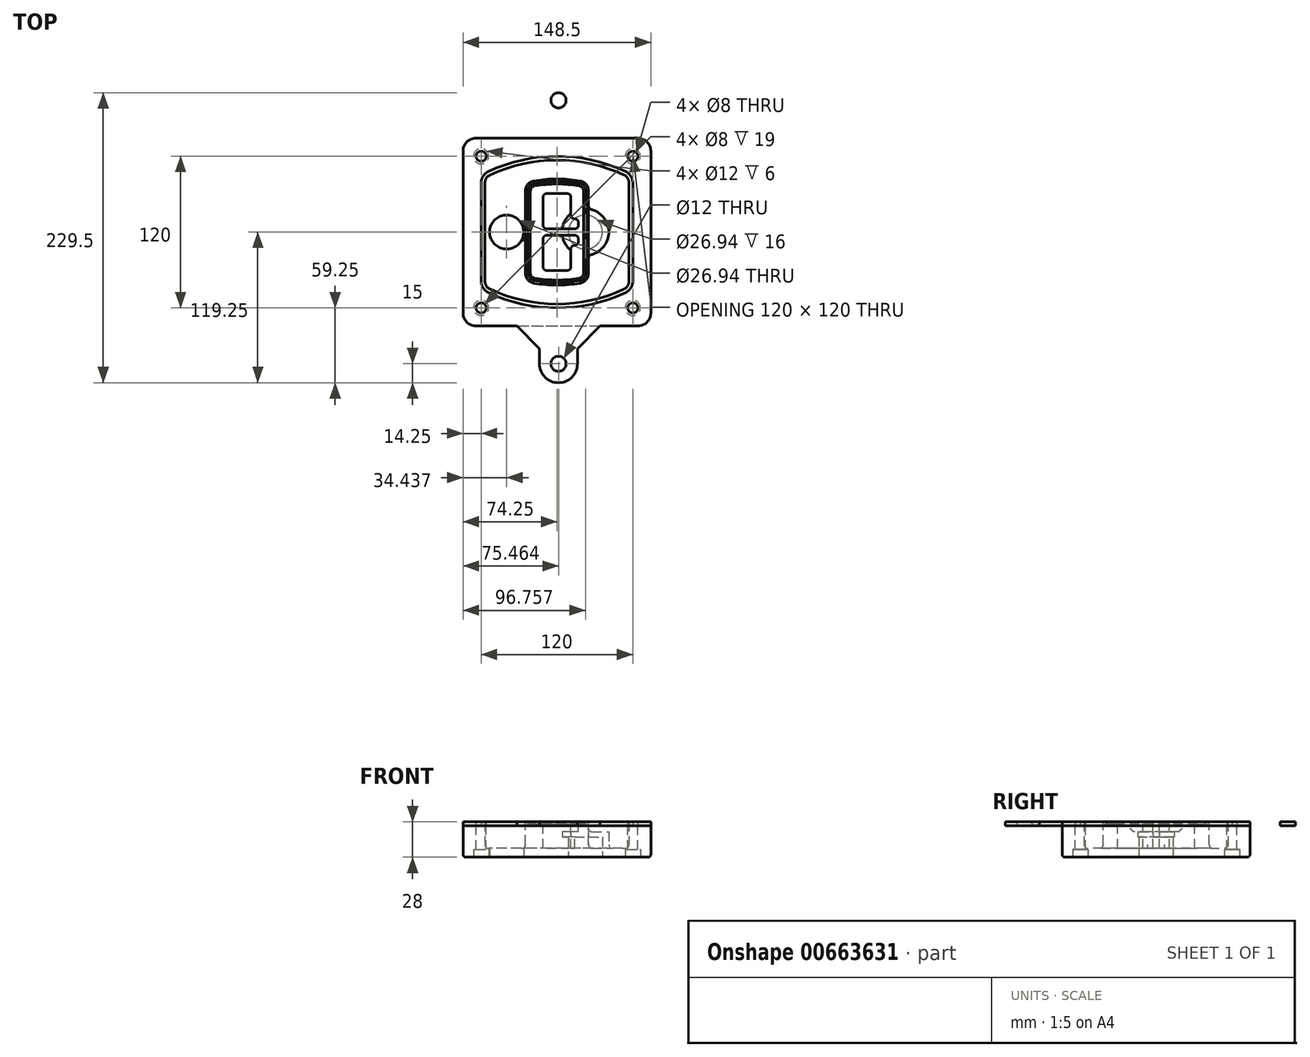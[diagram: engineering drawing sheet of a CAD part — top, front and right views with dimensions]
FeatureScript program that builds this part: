
annotation { "Feature Type Name" : "Feature", "Feature Type Description" : "" }
export const myFeature = defineFeature(function(context is Context, id is Id, definition is map)
    precondition{}
    {
        {
            var Q0;
            Q0=qCreatedBy(makeId("Top.planeOp"),FACE);
            var sketch = newSketch(context, id + "F0", { "sketchPlane" : qUnion([Q0])});
            skPoint(sketch, "E0.rect.middle", {"position": v(0, 0) * mm});
            skLineSegment(sketch, "E1.bottom", {"start": v(-64.25, -74.25) * mm, "end": v(64.25, -74.25) * mm});
            skLineSegment(sketch, "E1.top", {"start": v(-64.25, 74.25) * mm, "end": v(64.25, 74.25) * mm});
            skLineSegment(sketch, "E1.left", {"start": v(-74.25, -64.25) * mm, "end": v(-74.25, 64.25) * mm});
            skLineSegment(sketch, "E1.right", {"start": v(74.25, -64.25) * mm, "end": v(74.25, 64.25) * mm});
            skLineSegment(sketch, "E2", {"start": v(-74.25, 74.25) * mm, "end": v(74.25, -74.25) * mm, "construction": true});
            skLineSegment(sketch, "E3", {"start": v(74.25, 74.25) * mm, "end": v(-74.25, -74.25) * mm, "construction": true});
            skCircle(sketch, "E4", {"center": v(-60, 60) * mm, "radius": 4 * mm});
            skCircle(sketch, "E5", {"center": v(60, 60) * mm, "radius": 4 * mm});
            skCircle(sketch, "E6", {"center": v(60, -60) * mm, "radius": 4 * mm});
            skCircle(sketch, "E7", {"center": v(-60, -60) * mm, "radius": 4 * mm});
            skLineSegment(sketch, "E8", {"start": v(-60, 60) * mm, "end": v(60, 60) * mm, "construction": true});
            skLineSegment(sketch, "E9", {"start": v(60, 60) * mm, "end": v(60, -60) * mm, "construction": true});
            skLineSegment(sketch, "E10", {"start": v(60, -60) * mm, "end": v(-60, -60) * mm, "construction": true});
            skLineSegment(sketch, "E11", {"start": v(-60, -60) * mm, "end": v(-60, 60) * mm, "construction": true});
            skLineSegment(sketch, "E12", {"start": v(-60, 38.83) * mm, "end": v(-60, -38.83) * mm});
            skLineSegment(sketch, "E13", {"start": v(60, 38.83) * mm, "end": v(60, -38.83) * mm});
            skArc(sketch, "E14", {"start": v(54.26, 47.88) * mm, "mid": v(0, 60) * mm, "end": v(-54.26, 47.88) * mm});
            skArc(sketch, "E15", {"start": v(-54.26, -47.88) * mm, "mid": v(0, -60) * mm, "end": v(54.26, -47.88) * mm});
            skLineSegment(sketch, "E16", {"start": v(-60, 0) * mm, "end": v(60, 0) * mm, "construction": true});
            skPoint(sketch, "E17.visualSharp", {"position": v(-60, -45) * mm});
            skArc(sketch, "E17.filletArc", {"start": v(-60, -38.83) * mm, "mid": v(-58.44, -44.2) * mm, "end": v(-54.26, -47.88) * mm});
            skPoint(sketch, "E18.visualSharp", {"position": v(-60, 45) * mm});
            skArc(sketch, "E18.filletArc", {"start": v(-54.26, 47.88) * mm, "mid": v(-58.44, 44.2) * mm, "end": v(-60, 38.83) * mm});
            skPoint(sketch, "E19.visualSharp", {"position": v(60, 45) * mm});
            skArc(sketch, "E19.filletArc", {"start": v(60, 38.83) * mm, "mid": v(58.44, 44.2) * mm, "end": v(54.26, 47.88) * mm});
            skPoint(sketch, "E20.visualSharp", {"position": v(60, -45) * mm});
            skArc(sketch, "E20.filletArc", {"start": v(54.26, -47.88) * mm, "mid": v(58.44, -44.2) * mm, "end": v(60, -38.83) * mm});
            skPoint(sketch, "E21.visualSharp", {"position": v(-74.25, 74.25) * mm});
            skArc(sketch, "E21.filletArc", {"start": v(-64.25, 74.25) * mm, "mid": v(-71.32, 71.32) * mm, "end": v(-74.25, 64.25) * mm});
            skPoint(sketch, "E22.visualSharp", {"position": v(74.25, 74.25) * mm});
            skArc(sketch, "E22.filletArc", {"start": v(74.25, 64.25) * mm, "mid": v(71.32, 71.32) * mm, "end": v(64.25, 74.25) * mm});
            skPoint(sketch, "E23.visualSharp", {"position": v(74.25, -74.25) * mm});
            skArc(sketch, "E23.filletArc", {"start": v(64.25, -74.25) * mm, "mid": v(71.32, -71.32) * mm, "end": v(74.25, -64.25) * mm});
            skPoint(sketch, "E24.visualSharp", {"position": v(-74.25, -74.25) * mm});
            skArc(sketch, "E24.filletArc", {"start": v(-74.25, -64.25) * mm, "mid": v(-71.32, -71.32) * mm, "end": v(-64.25, -74.25) * mm});
            skArc(sketch, "E25.0", {"start": v(57, 38.83) * mm, "mid": v(55.9, 42.58) * mm, "end": v(52.98, 45.17) * mm});
            skLineSegment(sketch, "E25.1", {"start": v(57, 38.83) * mm, "end": v(57, -38.83) * mm});
            skArc(sketch, "E25.2", {"start": v(52.98, -45.17) * mm, "mid": v(55.9, -42.58) * mm, "end": v(57, -38.83) * mm});
            skArc(sketch, "E25.3", {"start": v(-52.98, -45.17) * mm, "mid": v(0, -57) * mm, "end": v(52.98, -45.17) * mm});
            skArc(sketch, "E25.4", {"start": v(-57, -38.83) * mm, "mid": v(-55.9, -42.58) * mm, "end": v(-52.98, -45.17) * mm});
            skArc(sketch, "E25.5", {"start": v(52.98, 45.17) * mm, "mid": v(0, 57) * mm, "end": v(-52.98, 45.17) * mm});
            skLineSegment(sketch, "E25.6", {"start": v(-57, 38.83) * mm, "end": v(-57, -38.83) * mm});
            skArc(sketch, "E25.7", {"start": v(-52.98, 45.17) * mm, "mid": v(-55.9, 42.58) * mm, "end": v(-57, 38.83) * mm});
            skArc(sketch, "E26.0", {"start": v(-55.96, 51.5) * mm, "mid": v(-61.82, 46.33) * mm, "end": v(-64, 38.83) * mm});
            skArc(sketch, "E26.1", {"start": v(55.96, 51.5) * mm, "mid": v(0, 64) * mm, "end": v(-55.96, 51.5) * mm});
            skArc(sketch, "E26.2", {"start": v(64, 38.83) * mm, "mid": v(61.82, 46.33) * mm, "end": v(55.96, 51.5) * mm});
            skLineSegment(sketch, "E26.3", {"start": v(64, 38.83) * mm, "end": v(64, -38.83) * mm});
            skArc(sketch, "E26.4", {"start": v(55.96, -51.5) * mm, "mid": v(61.82, -46.33) * mm, "end": v(64, -38.83) * mm});
            skLineSegment(sketch, "E26.5", {"start": v(-64, 38.83) * mm, "end": v(-64, -38.83) * mm});
            skArc(sketch, "E26.6", {"start": v(-55.96, -51.5) * mm, "mid": v(0, -64) * mm, "end": v(55.96, -51.5) * mm});
            skArc(sketch, "E26.7", {"start": v(-64, -38.83) * mm, "mid": v(-61.82, -46.33) * mm, "end": v(-55.96, -51.5) * mm});
            skSolve(sketch);
        }
        {
            var Q0;
            Q0=makeQuery(id+"F0.imprint","IMPRINT",FACE,{"disambiguationData":[TD([[makeQuery(id+"F0.imprint","IMPRINT",EDGE,{"derivedFrom":sQuery(id+"F0.wireOp",EDGE,"E1.bottom")}),1.0]])]});
            var Q1;
            Q1=makeQuery(id+"F0.imprint","IMPRINT",FACE,{"disambiguationData":[TD([[makeQuery(id+"F0.imprint","IMPRINT",EDGE,{"derivedFrom":sQuery(id+"F0.wireOp",EDGE,"E12")}),1.0]])]});
            var Q2;
            Q2=makeQuery(id+"F0.imprint","IMPRINT",FACE,{"disambiguationData":[TD([[makeQuery(id+"F0.imprint","IMPRINT",EDGE,{"derivedFrom":sQuery(id+"F0.wireOp",EDGE,"E25.0")}),1.0]])]});
            var Q3;
            Q3=makeQuery(id+"F0.imprint","IMPRINT",FACE,{"disambiguationData":[TD([[makeQuery(id+"F0.imprint","IMPRINT",EDGE,{"derivedFrom":sQuery(id+"F0.wireOp",EDGE,"E12")}),-1.0]])]});
            extrude(context, id + "F1", {"entities" : qUnion([Q0, Q1, Q2, Q3]), "oppositeDirection" : true, "depth" : 25 * mm});
        }
        {
            var Q0;
            Q0=makeQuery(id+"F0.imprint","IMPRINT",FACE,{"disambiguationData":[TD([[makeQuery(id+"F0.imprint","IMPRINT",EDGE,{"derivedFrom":sQuery(id+"F0.wireOp",EDGE,"E12")}),1.0]])]});
            extrude(context, id + "F2", {"entities" : qUnion([Q0]), "operationType" : NewBodyOperationType.ADD, "depth" : 3 * mm});
        }
        {
            var Q0;
            Q0=makeQuery(id+"F0.imprint","IMPRINT",FACE,{"disambiguationData":[TD([[makeQuery(id+"F0.imprint","IMPRINT",EDGE,{"derivedFrom":sQuery(id+"F0.wireOp",EDGE,"E25.0")}),1.0]])]});
            extrude(context, id + "F3", {"entities" : qUnion([Q0]), "operationType" : NewBodyOperationType.REMOVE, "oppositeDirection" : true, "depth" : 18 * mm});
        }
        {
            var Q0;
            Q0=makeQuery(id+"F2.opExtrude","CAP_FACE",FACE,{"disambiguationData":[OSD([sQuery(id+"F0.wireOp",EDGE,"E12"),sQuery(id+"F0.wireOp",EDGE,"E13"),sQuery(id+"F0.wireOp",EDGE,"E14"),sQuery(id+"F0.wireOp",EDGE,"E15"),sQuery(id+"F0.wireOp",EDGE,"E17.filletArc"),sQuery(id+"F0.wireOp",EDGE,"E18.filletArc"),sQuery(id+"F0.wireOp",EDGE,"E19.filletArc"),sQuery(id+"F0.wireOp",EDGE,"E20.filletArc"),sQuery(id+"F0.wireOp",EDGE,"E25.0"),sQuery(id+"F0.wireOp",EDGE,"E25.1"),sQuery(id+"F0.wireOp",EDGE,"E25.2"),sQuery(id+"F0.wireOp",EDGE,"E25.3"),sQuery(id+"F0.wireOp",EDGE,"E25.4"),sQuery(id+"F0.wireOp",EDGE,"E25.5"),sQuery(id+"F0.wireOp",EDGE,"E25.6"),sQuery(id+"F0.wireOp",EDGE,"E25.7")])],"isStart":false});
            var sketch = newSketch(context, id + "F4", { "sketchPlane" : qUnion([Q0])});
            skArc(sketch, "E27.0", {"start": v(-18.34, -40.45) * mm, "mid": v(0, -42) * mm, "end": v(18.34, -40.45) * mm});
            skArc(sketch, "E28.0", {"start": v(18.34, 40.45) * mm, "mid": v(0, 42) * mm, "end": v(-18.34, 40.45) * mm});
            skLineSegment(sketch, "E29", {"start": v(-25, 32.57) * mm, "end": v(-25, -32.57) * mm});
            skLineSegment(sketch, "E30", {"start": v(25, 32.57) * mm, "end": v(25, -32.57) * mm});
            skLineSegment(sketch, "E31", {"start": v(-25, 39.1) * mm, "end": v(25, 39.1) * mm, "construction": true});
            skLineSegment(sketch, "E32", {"start": v(-25, -39.1) * mm, "end": v(25, -39.1) * mm, "construction": true});
            skPoint(sketch, "E33.visualSharp", {"position": v(-25, 39.1) * mm});
            skArc(sketch, "E33.filletArc", {"start": v(-18.34, 40.45) * mm, "mid": v(-23.11, 37.73) * mm, "end": v(-25, 32.57) * mm});
            skPoint(sketch, "E34.visualSharp", {"position": v(25, 39.1) * mm});
            skArc(sketch, "E34.filletArc", {"start": v(25, 32.57) * mm, "mid": v(23.11, 37.73) * mm, "end": v(18.34, 40.45) * mm});
            skPoint(sketch, "E35.visualSharp", {"position": v(25, -39.1) * mm});
            skArc(sketch, "E35.filletArc", {"start": v(18.34, -40.45) * mm, "mid": v(23.11, -37.73) * mm, "end": v(25, -32.57) * mm});
            skPoint(sketch, "E36.visualSharp", {"position": v(-25, -39.1) * mm});
            skArc(sketch, "E36.filletArc", {"start": v(-25, -32.57) * mm, "mid": v(-23.11, -37.73) * mm, "end": v(-18.34, -40.45) * mm});
            skArc(sketch, "E37.0", {"start": v(52.98, 45.17) * mm, "mid": v(0, 57) * mm, "end": v(-52.98, 45.17) * mm});
            skArc(sketch, "E37.1", {"start": v(-52.98, 45.17) * mm, "mid": v(-55.9, 42.58) * mm, "end": v(-57, 38.83) * mm});
            skLineSegment(sketch, "E37.2", {"start": v(-57, 38.83) * mm, "end": v(-57, -38.83) * mm});
            skArc(sketch, "E37.3", {"start": v(-57, -38.83) * mm, "mid": v(-55.9, -42.58) * mm, "end": v(-52.98, -45.17) * mm});
            skArc(sketch, "E37.4", {"start": v(-52.98, -45.17) * mm, "mid": v(0, -57) * mm, "end": v(52.98, -45.17) * mm});
            skArc(sketch, "E37.5", {"start": v(52.98, -45.17) * mm, "mid": v(55.9, -42.58) * mm, "end": v(57, -38.83) * mm});
            skLineSegment(sketch, "E37.6", {"start": v(57, 38.83) * mm, "end": v(57, -38.83) * mm});
            skArc(sketch, "E37.7", {"start": v(57, 38.83) * mm, "mid": v(55.9, 42.58) * mm, "end": v(52.98, 45.17) * mm});
            skLineSegment(sketch, "E38.0", {"start": v(23, 32.57) * mm, "end": v(23, -32.57) * mm});
            skArc(sketch, "E38.1", {"start": v(18, -38.48) * mm, "mid": v(21.58, -36.44) * mm, "end": v(23, -32.57) * mm});
            skArc(sketch, "E38.2", {"start": v(-18, -38.48) * mm, "mid": v(0, -40) * mm, "end": v(18, -38.48) * mm});
            skArc(sketch, "E38.3", {"start": v(-23, -32.57) * mm, "mid": v(-21.58, -36.44) * mm, "end": v(-18, -38.48) * mm});
            skLineSegment(sketch, "E38.4", {"start": v(-23, 32.57) * mm, "end": v(-23, -32.57) * mm});
            skArc(sketch, "E38.5", {"start": v(23, 32.57) * mm, "mid": v(21.58, 36.44) * mm, "end": v(18, 38.48) * mm});
            skArc(sketch, "E38.6", {"start": v(-18, 38.48) * mm, "mid": v(-21.58, 36.44) * mm, "end": v(-23, 32.57) * mm});
            skArc(sketch, "E38.7", {"start": v(18, 38.48) * mm, "mid": v(0, 40) * mm, "end": v(-18, 38.48) * mm});
            skArc(sketch, "E39.0", {"start": v(21, 32.57) * mm, "mid": v(20.06, 35.15) * mm, "end": v(17.67, 36.5) * mm});
            skLineSegment(sketch, "E39.1", {"start": v(21, 32.57) * mm, "end": v(21, -32.57) * mm});
            skArc(sketch, "E39.2", {"start": v(17.67, -36.5) * mm, "mid": v(20.06, -35.15) * mm, "end": v(21, -32.57) * mm});
            skArc(sketch, "E39.3", {"start": v(-17.67, -36.5) * mm, "mid": v(0, -38) * mm, "end": v(17.67, -36.5) * mm});
            skArc(sketch, "E39.4", {"start": v(-21, -32.57) * mm, "mid": v(-20.06, -35.15) * mm, "end": v(-17.67, -36.5) * mm});
            skArc(sketch, "E39.5", {"start": v(17.67, 36.5) * mm, "mid": v(0, 38) * mm, "end": v(-17.67, 36.5) * mm});
            skLineSegment(sketch, "E39.6", {"start": v(-21, 32.57) * mm, "end": v(-21, -32.57) * mm});
            skArc(sketch, "E39.7", {"start": v(-17.67, 36.5) * mm, "mid": v(-20.06, 35.15) * mm, "end": v(-21, 32.57) * mm});
            skLineSegment(sketch, "E40", {"start": v(-25, 0) * mm, "end": v(25, 0) * mm, "construction": true});
            skLineSegment(sketch, "E41", {"start": v(-11, 5.5) * mm, "end": v(-11, 27.5) * mm});
            skLineSegment(sketch, "E42", {"start": v(-8, 30.5) * mm, "end": v(8, 30.5) * mm});
            skLineSegment(sketch, "E43", {"start": v(11, 27.5) * mm, "end": v(11, 13.5) * mm});
            skLineSegment(sketch, "E44", {"start": v(14, 10.5) * mm, "end": v(14, 10.5) * mm});
            skLineSegment(sketch, "E45", {"start": v(17, 7.5) * mm, "end": v(17, 5.5) * mm});
            skLineSegment(sketch, "E46", {"start": v(14, 2.5) * mm, "end": v(-8, 2.5) * mm});
            skPoint(sketch, "E47.visualSharp", {"position": v(-11, 30.5) * mm});
            skArc(sketch, "E47.filletArc", {"start": v(-8, 30.5) * mm, "mid": v(-10.12, 29.62) * mm, "end": v(-11, 27.5) * mm});
            skPoint(sketch, "E48.visualSharp", {"position": v(11, 30.5) * mm});
            skArc(sketch, "E48.filletArc", {"start": v(11, 27.5) * mm, "mid": v(10.12, 29.62) * mm, "end": v(8, 30.5) * mm});
            skPoint(sketch, "E49.visualSharp", {"position": v(11, 10.5) * mm});
            skArc(sketch, "E49.filletArc", {"start": v(11, 13.5) * mm, "mid": v(11.88, 11.38) * mm, "end": v(14, 10.5) * mm});
            skPoint(sketch, "E50.visualSharp", {"position": v(17, 10.5) * mm});
            skArc(sketch, "E50.filletArc", {"start": v(17, 7.5) * mm, "mid": v(16.12, 9.62) * mm, "end": v(14, 10.5) * mm});
            skPoint(sketch, "E51.visualSharp", {"position": v(17, 2.5) * mm});
            skArc(sketch, "E51.filletArc", {"start": v(14, 2.5) * mm, "mid": v(16.12, 3.38) * mm, "end": v(17, 5.5) * mm});
            skPoint(sketch, "E52.visualSharp", {"position": v(-11, 2.5) * mm});
            skArc(sketch, "E52.filletArc", {"start": v(-11, 5.5) * mm, "mid": v(-10.12, 3.38) * mm, "end": v(-8, 2.5) * mm});
            skLineSegment(sketch, "E53.0.MirrorCS", {"start": v(14, -2.5) * mm, "end": v(-8, -2.5) * mm});
            skArc(sketch, "E54.0.MirrorCS", {"start": v(-11, -5.5) * mm, "mid": v(-10.12, -3.38) * mm, "end": v(-8, -2.5) * mm});
            skLineSegment(sketch, "E55.0.MirrorCS", {"start": v(-11, -5.5) * mm, "end": v(-11, -27.5) * mm});
            skArc(sketch, "E56.0.MirrorCS", {"start": v(-8, -30.5) * mm, "mid": v(-10.12, -29.62) * mm, "end": v(-11, -27.5) * mm});
            skLineSegment(sketch, "E57.0.MirrorCS", {"start": v(-8, -30.5) * mm, "end": v(8, -30.5) * mm});
            skArc(sketch, "E58.0.MirrorCS", {"start": v(11, -27.5) * mm, "mid": v(10.12, -29.62) * mm, "end": v(8, -30.5) * mm});
            skLineSegment(sketch, "E59.0.MirrorCS", {"start": v(11, -27.5) * mm, "end": v(11, -13.5) * mm});
            skArc(sketch, "E60.0.MirrorCS", {"start": v(11, -13.5) * mm, "mid": v(11.88, -11.38) * mm, "end": v(14, -10.5) * mm});
            skArc(sketch, "E61.0.MirrorCS", {"start": v(17, -7.5) * mm, "mid": v(16.12, -9.62) * mm, "end": v(14, -10.5) * mm});
            skLineSegment(sketch, "E62.0.MirrorCS", {"start": v(17, -7.5) * mm, "end": v(17, -5.5) * mm});
            skArc(sketch, "E63.0.MirrorCS", {"start": v(14, -2.5) * mm, "mid": v(16.12, -3.38) * mm, "end": v(17, -5.5) * mm});
            skSolve(sketch);
        }
        {
            var Q0;
            Q0=makeQuery(id+"F4.imprint","IMPRINT",FACE,{"disambiguationData":[TD([[makeQuery(id+"F4.imprint","IMPRINT",EDGE,{"derivedFrom":sQuery(id+"F4.wireOp",EDGE,"E27.0")}),1.0]])]});
            var Q1;
            Q1=makeQuery(id+"F4.imprint","IMPRINT",FACE,{"disambiguationData":[TD([[makeQuery(id+"F4.imprint","IMPRINT",EDGE,{"derivedFrom":sQuery(id+"F4.wireOp",EDGE,"E38.0")}),-1.0]])]});
            var Q2;
            Q2=makeQuery(id+"F4.imprint","IMPRINT",FACE,{"disambiguationData":[TD([[makeQuery(id+"F4.imprint","IMPRINT",EDGE,{"derivedFrom":sQuery(id+"F4.wireOp",EDGE,"E39.0")}),1.0]])]});
            extrude(context, id + "F5", {"entities" : qUnion([Q0, Q1, Q2]), "operationType" : NewBodyOperationType.ADD, "endBound" : BoundingType.UP_TO_NEXT, "oppositeDirection" : true, "depth" : 25 * mm});
        }
        {
            var Q0;
            Q0=makeQuery(id+"F4.imprint","IMPRINT",FACE,{"disambiguationData":[TD([[makeQuery(id+"F4.imprint","IMPRINT",EDGE,{"derivedFrom":sQuery(id+"F4.wireOp",EDGE,"E38.0")}),-1.0]])]});
            extrude(context, id + "F6", {"entities" : qUnion([Q0]), "operationType" : NewBodyOperationType.REMOVE, "oppositeDirection" : true, "depth" : 2 * mm});
        }
        {
            var Q0;
            Q0=makeQuery(id+"F1.opExtrude","CAP_FACE",FACE,{"disambiguationData":[OSD([sQuery(id+"F0.wireOp",EDGE,"E1.bottom"),sQuery(id+"F0.wireOp",EDGE,"E1.top"),sQuery(id+"F0.wireOp",EDGE,"E1.left"),sQuery(id+"F0.wireOp",EDGE,"E1.right"),sQuery(id+"F0.wireOp",EDGE,"E4"),sQuery(id+"F0.wireOp",EDGE,"E5"),sQuery(id+"F0.wireOp",EDGE,"E6"),sQuery(id+"F0.wireOp",EDGE,"E7"),sQuery(id+"F0.wireOp",EDGE,"E21.filletArc"),sQuery(id+"F0.wireOp",EDGE,"E22.filletArc"),sQuery(id+"F0.wireOp",EDGE,"E23.filletArc"),sQuery(id+"F0.wireOp",EDGE,"E24.filletArc")])],"isStart":false});
            var sketch = newSketch(context, id + "F7", { "sketchPlane" : qUnion([Q0])});
            skCircle(sketch, "E64", {"center": v(22.5, 0) * mm, "radius": 13.47 * mm});
            skCircle(sketch, "E65", {"center": v(-39.81, 0) * mm, "radius": 13.47 * mm});
            skLineSegment(sketch, "E66", {"start": v(74.25, 0) * mm, "end": v(-74.25, 0) * mm});
            skCircle(sketch, "E67", {"center": v(22.5, 0) * mm, "radius": 18.47 * mm});
            skCircle(sketch, "E68", {"center": v(60, -60) * mm, "radius": 6 * mm});
            skCircle(sketch, "E69", {"center": v(-60, -60) * mm, "radius": 6 * mm});
            skCircle(sketch, "E70", {"center": v(-60, 60) * mm, "radius": 6 * mm});
            skCircle(sketch, "E71", {"center": v(60, 60) * mm, "radius": 6 * mm});
            skSolve(sketch);
        }
        {
            var Q0;
            {var subQ1=sQuery(id+"F7.wireOp",EDGE,"E66");var subQ4=sQuery(id+"F7.wireOp",EDGE,"E64");var subQ6=makeQuery(id+"F7.imprint","INTERSECT",VERTEX,{"disambiguationData":[OD(0.0)],"derivedFrom":[subQ4,subQ1]});Q0=makeQuery(id+"F7.imprint","IMPRINT",FACE,{"disambiguationData":[TD([[makeQuery(id+"F7.imprint","IMPRINT",EDGE,{"disambiguationData":[TD([[subQ6,-1.0]])],"derivedFrom":subQ4}),-1.0]])]});}
            var Q1;
            {var subQ0=sQuery(id+"F7.wireOp",EDGE,"E66");var subQ1=sQuery(id+"F7.wireOp",EDGE,"E64");var subQ3=makeQuery(id+"F7.imprint","INTERSECT",VERTEX,{"disambiguationData":[OD(0.0)],"derivedFrom":[subQ1,subQ0]});Q1=makeQuery(id+"F7.imprint","IMPRINT",FACE,{"disambiguationData":[TD([[makeQuery(id+"F7.imprint","IMPRINT",EDGE,{"disambiguationData":[TD([[subQ3,-1.0]])],"derivedFrom":subQ1}),1.0]])]});}
            var Q2;
            {var subQ0=sQuery(id+"F7.wireOp",EDGE,"E66");var subQ1=sQuery(id+"F7.wireOp",EDGE,"E64");var subQ3=makeQuery(id+"F7.imprint","INTERSECT",VERTEX,{"disambiguationData":[OD(0.0)],"derivedFrom":[subQ1,subQ0]});Q2=makeQuery(id+"F7.imprint","IMPRINT",FACE,{"disambiguationData":[TD([[makeQuery(id+"F7.imprint","IMPRINT",EDGE,{"disambiguationData":[TD([[subQ3,1.0]])],"derivedFrom":subQ1}),1.0]])]});}
            var Q3;
            {var subQ1=sQuery(id+"F7.wireOp",EDGE,"E66");var subQ4=sQuery(id+"F7.wireOp",EDGE,"E64");var subQ6=makeQuery(id+"F7.imprint","INTERSECT",VERTEX,{"disambiguationData":[OD(0.0)],"derivedFrom":[subQ4,subQ1]});Q3=makeQuery(id+"F7.imprint","IMPRINT",FACE,{"disambiguationData":[TD([[makeQuery(id+"F7.imprint","IMPRINT",EDGE,{"disambiguationData":[TD([[subQ6,1.0]])],"derivedFrom":subQ4}),-1.0]])]});}
            extrude(context, id + "F8", {"entities" : qUnion([Q0, Q1, Q2, Q3]), "operationType" : NewBodyOperationType.ADD, "oppositeDirection" : true, "depth" : 20 * mm});
        }
        {
            var Q0;
            {var subQ0=sQuery(id+"F7.wireOp",EDGE,"E66");var subQ1=sQuery(id+"F7.wireOp",EDGE,"E64");var subQ3=makeQuery(id+"F7.imprint","INTERSECT",VERTEX,{"disambiguationData":[OD(0.0)],"derivedFrom":[subQ1,subQ0]});Q0=makeQuery(id+"F7.imprint","IMPRINT",FACE,{"disambiguationData":[TD([[makeQuery(id+"F7.imprint","IMPRINT",EDGE,{"disambiguationData":[TD([[subQ3,-1.0]])],"derivedFrom":subQ1}),1.0]])]});}
            var Q1;
            {var subQ0=sQuery(id+"F7.wireOp",EDGE,"E66");var subQ1=sQuery(id+"F7.wireOp",EDGE,"E64");var subQ3=makeQuery(id+"F7.imprint","INTERSECT",VERTEX,{"disambiguationData":[OD(0.0)],"derivedFrom":[subQ1,subQ0]});Q1=makeQuery(id+"F7.imprint","IMPRINT",FACE,{"disambiguationData":[TD([[makeQuery(id+"F7.imprint","IMPRINT",EDGE,{"disambiguationData":[TD([[subQ3,1.0]])],"derivedFrom":subQ1}),1.0]])]});}
            extrude(context, id + "F9", {"entities" : qUnion([Q0, Q1]), "operationType" : NewBodyOperationType.REMOVE, "oppositeDirection" : true, "depth" : 16 * mm});
        }
        {
            var Q0;
            {var subQ0=sQuery(id+"F7.wireOp",EDGE,"E66");var subQ1=sQuery(id+"F7.wireOp",EDGE,"E65");var subQ3=makeQuery(id+"F7.imprint","INTERSECT",VERTEX,{"disambiguationData":[OD(0.0)],"derivedFrom":[subQ1,subQ0]});Q0=makeQuery(id+"F7.imprint","IMPRINT",FACE,{"disambiguationData":[TD([[makeQuery(id+"F7.imprint","IMPRINT",EDGE,{"disambiguationData":[TD([[subQ3,-1.0]])],"derivedFrom":subQ1}),1.0]])]});}
            var Q1;
            {var subQ0=sQuery(id+"F7.wireOp",EDGE,"E66");var subQ1=sQuery(id+"F7.wireOp",EDGE,"E65");var subQ3=makeQuery(id+"F7.imprint","INTERSECT",VERTEX,{"disambiguationData":[OD(0.0)],"derivedFrom":[subQ1,subQ0]});Q1=makeQuery(id+"F7.imprint","IMPRINT",FACE,{"disambiguationData":[TD([[makeQuery(id+"F7.imprint","IMPRINT",EDGE,{"disambiguationData":[TD([[subQ3,1.0]])],"derivedFrom":subQ1}),1.0]])]});}
            extrude(context, id + "F10", {"entities" : qUnion([Q0, Q1]), "operationType" : NewBodyOperationType.REMOVE, "oppositeDirection" : true, "depth" : 25 * mm});
        }
        {
            var Q0;
            Q0=makeQuery(id+"F7.imprint","IMPRINT",FACE,{"disambiguationData":[TD([[makeQuery(id+"F7.imprint","IMPRINT",EDGE,{"derivedFrom":sQuery(id+"F7.wireOp",EDGE,"E68")}),1.0]])]});
            var Q1;
            Q1=makeQuery(id+"F7.imprint","IMPRINT",FACE,{"disambiguationData":[TD([[makeQuery(id+"F7.imprint","IMPRINT",EDGE,{"derivedFrom":makeQuery(id+"F1.opExtrude","CAP_EDGE",EDGE,{"disambiguationData":[OSD([sQuery(id+"F0.wireOp",EDGE,"E5")])],"isStart":false})}),-1.0]])]});
            var Q2;
            Q2=makeQuery(id+"F7.imprint","IMPRINT",FACE,{"disambiguationData":[TD([[makeQuery(id+"F7.imprint","IMPRINT",EDGE,{"derivedFrom":sQuery(id+"F7.wireOp",EDGE,"E69")}),1.0]])]});
            var Q3;
            Q3=makeQuery(id+"F7.imprint","IMPRINT",FACE,{"disambiguationData":[TD([[makeQuery(id+"F7.imprint","IMPRINT",EDGE,{"derivedFrom":makeQuery(id+"F1.opExtrude","CAP_EDGE",EDGE,{"disambiguationData":[OSD([sQuery(id+"F0.wireOp",EDGE,"E4")])],"isStart":false})}),-1.0]])]});
            var Q4;
            Q4=makeQuery(id+"F7.imprint","IMPRINT",FACE,{"disambiguationData":[TD([[makeQuery(id+"F7.imprint","IMPRINT",EDGE,{"derivedFrom":sQuery(id+"F7.wireOp",EDGE,"E70")}),1.0]])]});
            var Q5;
            Q5=makeQuery(id+"F7.imprint","IMPRINT",FACE,{"disambiguationData":[TD([[makeQuery(id+"F7.imprint","IMPRINT",EDGE,{"derivedFrom":makeQuery(id+"F1.opExtrude","CAP_EDGE",EDGE,{"disambiguationData":[OSD([sQuery(id+"F0.wireOp",EDGE,"E7")])],"isStart":false})}),-1.0]])]});
            var Q6;
            Q6=makeQuery(id+"F7.imprint","IMPRINT",FACE,{"disambiguationData":[TD([[makeQuery(id+"F7.imprint","IMPRINT",EDGE,{"derivedFrom":sQuery(id+"F7.wireOp",EDGE,"E71")}),1.0]])]});
            var Q7;
            Q7=makeQuery(id+"F7.imprint","IMPRINT",FACE,{"disambiguationData":[TD([[makeQuery(id+"F7.imprint","IMPRINT",EDGE,{"derivedFrom":makeQuery(id+"F1.opExtrude","CAP_EDGE",EDGE,{"disambiguationData":[OSD([sQuery(id+"F0.wireOp",EDGE,"E6")])],"isStart":false})}),-1.0]])]});
            extrude(context, id + "F11", {"entities" : qUnion([Q0, Q1, Q2, Q3, Q4, Q5, Q6, Q7]), "operationType" : NewBodyOperationType.REMOVE, "oppositeDirection" : true, "depth" : 6 * mm});
        }
        {
            var Q0;
            Q0=makeQuery(id+"F9.boolean.opBoolean","COPY",FACE,{"derivedFrom":makeQuery(id+"F9.opExtrude","CAP_FACE",FACE,{"disambiguationData":[OSD([sQuery(id+"F7.wireOp",EDGE,"E64")])],"isStart":false})});
            var sketch = newSketch(context, id + "F12", { "sketchPlane" : qUnion([Q0])});
            skArc(sketch, "E72.0", {"start": v(11, 14.45) * mm, "mid": v(6.45, 9.13) * mm, "end": v(4.2, 2.5) * mm});
            skArc(sketch, "E72.1", {"start": v(4.2, -2.5) * mm, "mid": v(6.45, -9.13) * mm, "end": v(11, -14.45) * mm});
            skLineSegment(sketch, "E73", {"start": v(4.2, -2.5) * mm, "end": v(14, -2.5) * mm});
            skLineSegment(sketch, "E74.0", {"start": v(14, 2.5) * mm, "end": v(4.2, 2.5) * mm});
            skArc(sketch, "E74.1", {"start": v(14, 2.5) * mm, "mid": v(16.12, 3.38) * mm, "end": v(17, 5.5) * mm});
            skLineSegment(sketch, "E74.2", {"start": v(17, 7.5) * mm, "end": v(17, 5.5) * mm});
            skArc(sketch, "E74.3", {"start": v(17, 7.5) * mm, "mid": v(16.12, 9.62) * mm, "end": v(14, 10.5) * mm});
            skArc(sketch, "E74.4", {"start": v(11, 13.5) * mm, "mid": v(11.88, 11.38) * mm, "end": v(14, 10.5) * mm});
            skLineSegment(sketch, "E74.5", {"start": v(11, 14.45) * mm, "end": v(11, 13.5) * mm});
            skLineSegment(sketch, "E74.7", {"start": v(14, -2.5) * mm, "end": v(4.2, -2.5) * mm});
            skArc(sketch, "E74.8", {"start": v(14, -2.5) * mm, "mid": v(16.12, -3.38) * mm, "end": v(17, -5.5) * mm});
            skLineSegment(sketch, "E74.9", {"start": v(17, -7.5) * mm, "end": v(17, -5.5) * mm});
            skArc(sketch, "E74.10", {"start": v(17, -7.5) * mm, "mid": v(16.12, -9.62) * mm, "end": v(14, -10.5) * mm});
            skArc(sketch, "E74.11", {"start": v(11, -13.5) * mm, "mid": v(11.88, -11.38) * mm, "end": v(14, -10.5) * mm});
            skLineSegment(sketch, "E74.12", {"start": v(11, -14.45) * mm, "end": v(11, -13.5) * mm});
            skPoint(sketch, "E75.orphan", {"position": v(11, -27.5) * mm});
            skPoint(sketch, "E76.orphan", {"position": v(-8, -2.5) * mm});
            skPoint(sketch, "E77.orphan", {"position": v(-8, 2.5) * mm});
            skPoint(sketch, "E78.orphan", {"position": v(11, 27.5) * mm});
            skSolve(sketch);
        }
        {
            var Q0;
            {var subQ7=sQuery(id+"F12.wireOp",EDGE,"E72.0");var subQ14=sQuery(id+"F12.wireOp",EDGE,"E72.1");var subQ16=sQuery(id+"F12.wireOp",EDGE,"E74.1");var subQ18=sQuery(id+"F12.wireOp",EDGE,"E74.8");Q0=qUnion([makeQuery(id+"F12.imprint","IMPRINT",FACE,{"disambiguationData":[TD([[makeQuery(id+"F12.imprint","IMPRINT",EDGE,{"derivedFrom":subQ7}),1.0]])]}),makeQuery(id+"F12.imprint","IMPRINT",FACE,{"disambiguationData":[TD([[makeQuery(id+"F12.imprint","IMPRINT",EDGE,{"derivedFrom":subQ14}),1.0]])]}),makeQuery(id+"F12.imprint","IMPRINT",FACE,{"disambiguationData":[TD([[makeQuery(id+"F12.imprint","IMPRINT",EDGE,{"derivedFrom":subQ16}),1.0]])]}),makeQuery(id+"F12.imprint","IMPRINT",FACE,{"disambiguationData":[TD([[makeQuery(id+"F12.imprint","IMPRINT",EDGE,{"derivedFrom":subQ18}),-1.0]])]})]);}
            var Q1;
            Q1=makeQuery(id+"F5.boolean.opBoolean","SPLIT",FACE,{"disambiguationData":[TD([makeQuery(id+"F5.opExtrude","SWEPT_FACE",FACE,{"disambiguationData":[OSD([sQuery(id+"F4.wireOp",EDGE,"E41")])]})])],"derivedFrom":makeQuery(id+"F3.boolean.opBoolean","COPY",FACE,{"derivedFrom":makeQuery(id+"F3.opExtrude","CAP_FACE",FACE,{"disambiguationData":[OSD([sQuery(id+"F0.wireOp",EDGE,"E25.0"),sQuery(id+"F0.wireOp",EDGE,"E25.1"),sQuery(id+"F0.wireOp",EDGE,"E25.2"),sQuery(id+"F0.wireOp",EDGE,"E25.3"),sQuery(id+"F0.wireOp",EDGE,"E25.4"),sQuery(id+"F0.wireOp",EDGE,"E25.5"),sQuery(id+"F0.wireOp",EDGE,"E25.6"),sQuery(id+"F0.wireOp",EDGE,"E25.7")])],"isStart":false})})});
            extrude(context, id + "F13", {"entities" : qUnion([Q0]), "operationType" : NewBodyOperationType.REMOVE, "endBound" : BoundingType.UP_TO_SURFACE, "endBoundEntityFace" : qUnion([Q1]), "depth" : 25 * mm});
        }
        {
            var Q0;
            Q0=makeQuery(id+"F3.boolean.opBoolean","COPY",EDGE,{"derivedFrom":makeQuery(id+"F3.opExtrude","CAP_EDGE",EDGE,{"disambiguationData":[OSD([sQuery(id+"F0.wireOp",EDGE,"E25.6")])],"isStart":false})});
            var Q1;
            Q1=makeQuery(id+"F8.boolean.opBoolean","INTERSECT",EDGE,{"derivedFrom":[makeQuery(id+"F5.opExtrude","SWEPT_FACE",FACE,{"disambiguationData":[OSD([sQuery(id+"F4.wireOp",EDGE,"E30")])]}),makeQuery(id+"F8.opExtrude","CAP_FACE",FACE,{"disambiguationData":[OSD([sQuery(id+"F7.wireOp",EDGE,"E67")])],"isStart":false})]});
            var Q2;
            Q2=makeQuery(id+"F8.boolean.opBoolean","INTERSECT",EDGE,{"disambiguationData":[OD(1.0)],"derivedFrom":[makeQuery(id+"F5.opExtrude","SWEPT_FACE",FACE,{"disambiguationData":[OSD([sQuery(id+"F4.wireOp",EDGE,"E30")])]}),makeQuery(id+"F8.opExtrude","SWEPT_FACE",FACE,{"disambiguationData":[OSD([sQuery(id+"F7.wireOp",EDGE,"E67")])]})]});
            var Q3;
            {var subQ0=sQuery(id+"F4.wireOp",EDGE,"E30");Q3=makeQuery(id+"F8.boolean.opBoolean","SPLIT",EDGE,{"disambiguationData":[TD([makeQuery(id+"F5.opExtrude","SWEPT_FACE",FACE,{"disambiguationData":[OSD([sQuery(id+"F4.wireOp",EDGE,"E35.filletArc")])]})])],"derivedFrom":makeQuery(id+"F5.opExtrude","CAP_EDGE",EDGE,{"disambiguationData":[OSD([subQ0])],"isStart":false})});}
            var Q4;
            {var subQ0=sQuery(id+"F0.wireOp",EDGE,"E25.7");var subQ1=sQuery(id+"F0.wireOp",EDGE,"E25.1");var subQ2=sQuery(id+"F0.wireOp",EDGE,"E25.6");var subQ3=sQuery(id+"F0.wireOp",EDGE,"E25.5");var subQ4=sQuery(id+"F0.wireOp",EDGE,"E25.4");var subQ5=sQuery(id+"F0.wireOp",EDGE,"E25.0");var subQ6=sQuery(id+"F0.wireOp",EDGE,"E25.2");var subQ7=sQuery(id+"F0.wireOp",EDGE,"E25.3");Q4=makeQuery(id+"F8.boolean.opBoolean","INTERSECT",EDGE,{"derivedFrom":[makeQuery(id+"F5.boolean.opBoolean","SPLIT",FACE,{"disambiguationData":[TD([makeQuery(id+"F2.opExtrude","SWEPT_FACE",FACE,{"disambiguationData":[OSD([subQ5])]})])],"derivedFrom":makeQuery(id+"F3.boolean.opBoolean","COPY",FACE,{"derivedFrom":makeQuery(id+"F3.opExtrude","CAP_FACE",FACE,{"disambiguationData":[OSD([subQ5,subQ1,subQ6,subQ7,subQ4,subQ3,subQ2,subQ0])],"isStart":false})})}),makeQuery(id+"F8.opExtrude","SWEPT_FACE",FACE,{"disambiguationData":[OSD([sQuery(id+"F7.wireOp",EDGE,"E67")])]})]});}
            var Q5;
            Q5=makeQuery(id+"F8.boolean.opBoolean","INTERSECT",EDGE,{"disambiguationData":[OD(0.0)],"derivedFrom":[makeQuery(id+"F5.opExtrude","SWEPT_FACE",FACE,{"disambiguationData":[OSD([sQuery(id+"F4.wireOp",EDGE,"E30")])]}),makeQuery(id+"F8.opExtrude","SWEPT_FACE",FACE,{"disambiguationData":[OSD([sQuery(id+"F7.wireOp",EDGE,"E67")])]})]});
            fillet(context, id + "F14", {"entities" : qUnion([Q0, Q1, Q2, Q3, Q4, Q5]), "radius" : 3 * mm, "tangentPropagation" : true, "allowEdgeOverflow" : false});
        }
        {
            var Q0;
            Q0=makeQuery(id+"F1.opExtrude","CAP_EDGE",EDGE,{"disambiguationData":[OSD([sQuery(id+"F0.wireOp",EDGE,"E1.bottom")])],"isStart":false});
            fillet(context, id + "F15", {"entities" : qUnion([Q0]), "radius" : 2 * mm, "tangentPropagation" : true, "allowEdgeOverflow" : false});
        }
        {
            var Q0;
            Q0=qCreatedBy(makeId("Top.planeOp"),FACE);
            var sketch = newSketch(context, id + "F16", { "sketchPlane" : qUnion([Q0])});
            skLineSegment(sketch, "E79.0", {"start": v(-64.25, 74.25) * mm, "end": v(64.25, 74.25) * mm});
            skArc(sketch, "E79.1", {"start": v(74.25, 64.25) * mm, "mid": v(71.32, 71.32) * mm, "end": v(64.25, 74.25) * mm});
            skLineSegment(sketch, "E79.2", {"start": v(74.25, -64.25) * mm, "end": v(74.25, 64.25) * mm});
            skArc(sketch, "E79.3", {"start": v(64.25, -74.25) * mm, "mid": v(71.32, -71.32) * mm, "end": v(74.25, -64.25) * mm});
            skLineSegment(sketch, "E79.4", {"start": v(-64.25, -74.25) * mm, "end": v(64.25, -74.25) * mm});
            skArc(sketch, "E79.5", {"start": v(-74.25, -64.25) * mm, "mid": v(-71.32, -71.32) * mm, "end": v(-64.25, -74.25) * mm});
            skLineSegment(sketch, "E79.6", {"start": v(-74.25, -64.25) * mm, "end": v(-74.25, 64.25) * mm});
            skArc(sketch, "E79.7", {"start": v(-64.25, 74.25) * mm, "mid": v(-71.32, 71.32) * mm, "end": v(-74.25, 64.25) * mm});
            skArc(sketch, "E79.8", {"start": v(54.26, 47.88) * mm, "mid": v(0, 60) * mm, "end": v(-54.26, 47.88) * mm});
            skArc(sketch, "E79.9", {"start": v(-54.26, 47.88) * mm, "mid": v(-58.44, 44.2) * mm, "end": v(-60, 38.83) * mm});
            skLineSegment(sketch, "E79.10", {"start": v(-60, 38.83) * mm, "end": v(-60, -38.83) * mm});
            skArc(sketch, "E79.11", {"start": v(-60, -38.83) * mm, "mid": v(-58.44, -44.2) * mm, "end": v(-54.26, -47.88) * mm});
            skArc(sketch, "E79.12", {"start": v(-54.26, -47.88) * mm, "mid": v(0, -60) * mm, "end": v(54.26, -47.88) * mm});
            skArc(sketch, "E79.13", {"start": v(54.26, -47.88) * mm, "mid": v(58.44, -44.2) * mm, "end": v(60, -38.83) * mm});
            skLineSegment(sketch, "E79.14", {"start": v(60, 38.83) * mm, "end": v(60, -38.83) * mm});
            skArc(sketch, "E79.15", {"start": v(60, 38.83) * mm, "mid": v(58.44, 44.2) * mm, "end": v(54.26, 47.88) * mm});
            skCircle(sketch, "E79.16", {"center": v(60, 60) * mm, "radius": 4 * mm});
            skCircle(sketch, "E79.17", {"center": v(-60, 60) * mm, "radius": 4 * mm});
            skCircle(sketch, "E79.18", {"center": v(-60, -60) * mm, "radius": 4 * mm});
            skCircle(sketch, "E79.19", {"center": v(60, -60) * mm, "radius": 4 * mm});
            skLineSegment(sketch, "E80", {"start": v(34.21, 74.25) * mm, "end": v(16.21, 92.25) * mm});
            skLineSegment(sketch, "E81", {"start": v(-31.79, 74.25) * mm, "end": v(-13.79, 92.25) * mm});
            skLineSegment(sketch, "E82", {"start": v(16.21, 92.25) * mm, "end": v(16.21, 104.25) * mm});
            skLineSegment(sketch, "E83", {"start": v(-13.79, 92.25) * mm, "end": v(-13.79, 104.25) * mm});
            skArc(sketch, "E84", {"start": v(16.21, 104.25) * mm, "mid": v(1.21, 119.25) * mm, "end": v(-13.79, 104.25) * mm});
            skLineSegment(sketch, "E85", {"start": v(1.21, 104.25) * mm, "end": v(1.21, 74.25) * mm, "construction": true});
            skCircle(sketch, "E86", {"center": v(1.21, 104.25) * mm, "radius": 6 * mm});
            skLineSegment(sketch, "E87", {"start": v(-74.25, 0) * mm, "end": v(74.25, 0) * mm, "construction": true});
            skArc(sketch, "E88.MirrorCS", {"start": v(-13.79, 104.25) * mm, "mid": v(1.21, 119.25) * mm, "end": v(16.21, 104.25) * mm});
            skLineSegment(sketch, "E89.MirrorCS", {"start": v(-13.79, -92.25) * mm, "end": v(-13.79, -104.25) * mm});
            skLineSegment(sketch, "E90.MirrorCS", {"start": v(16.21, -92.25) * mm, "end": v(16.21, -104.25) * mm});
            skCircle(sketch, "E91.MirrorC", {"center": v(1.21, -104.25) * mm, "radius": 6 * mm});
            skLineSegment(sketch, "E92.MirrorCS", {"start": v(34.21, -74.25) * mm, "end": v(16.21, -92.25) * mm});
            skArc(sketch, "E93.MirrorCS", {"start": v(-13.79, -104.25) * mm, "mid": v(1.21, -119.25) * mm, "end": v(16.21, -104.25) * mm});
            skLineSegment(sketch, "E94.MirrorCS", {"start": v(-31.79, -74.25) * mm, "end": v(-13.79, -92.25) * mm});
            skArc(sketch, "E95.MirrorCS", {"start": v(16.21, -104.25) * mm, "mid": v(1.21, -119.25) * mm, "end": v(-13.79, -104.25) * mm});
            skLineSegment(sketch, "E96.MirrorCS", {"start": v(1.21, -104.25) * mm, "end": v(1.21, -74.25) * mm, "construction": true});
            skSolve(sketch);
        }
        {
            var Q0;
            Q0=makeQuery(id+"F16.imprint","IMPRINT",FACE,{"disambiguationData":[TD([[makeQuery(id+"F16.imprint","IMPRINT",EDGE,{"derivedFrom":sQuery(id+"F16.wireOp",EDGE,"E90.MirrorCS")}),-1.0]])]});
            var Q1;
            {var subQ1=sQuery(id+"F16.wireOp",EDGE,"E79.1");Q1=makeQuery(id+"F16.imprint","IMPRINT",FACE,{"disambiguationData":[TD([[makeQuery(id+"F16.imprint","IMPRINT",EDGE,{"derivedFrom":subQ1}),1.0]])]});}
            var Q2;
            Q2=makeQuery(id+"F16.imprint","IMPRINT",FACE,{"disambiguationData":[TD([[makeQuery(id+"F16.imprint","IMPRINT",EDGE,{"derivedFrom":sQuery(id+"F16.wireOp",EDGE,"E86")}),1.0]])]});
            var Q3;
            Q3=makeQuery(id+"F2.opExtrude","CAP_FACE",FACE,{"disambiguationData":[OSD([sQuery(id+"F0.wireOp",EDGE,"E12"),sQuery(id+"F0.wireOp",EDGE,"E13"),sQuery(id+"F0.wireOp",EDGE,"E14"),sQuery(id+"F0.wireOp",EDGE,"E15"),sQuery(id+"F0.wireOp",EDGE,"E17.filletArc"),sQuery(id+"F0.wireOp",EDGE,"E18.filletArc"),sQuery(id+"F0.wireOp",EDGE,"E19.filletArc"),sQuery(id+"F0.wireOp",EDGE,"E20.filletArc"),sQuery(id+"F0.wireOp",EDGE,"E25.0"),sQuery(id+"F0.wireOp",EDGE,"E25.1"),sQuery(id+"F0.wireOp",EDGE,"E25.2"),sQuery(id+"F0.wireOp",EDGE,"E25.3"),sQuery(id+"F0.wireOp",EDGE,"E25.4"),sQuery(id+"F0.wireOp",EDGE,"E25.5"),sQuery(id+"F0.wireOp",EDGE,"E25.6"),sQuery(id+"F0.wireOp",EDGE,"E25.7")])],"isStart":false});
            extrude(context, id + "F17", {"entities" : qUnion([Q0, Q1, Q2]), "endBound" : BoundingType.UP_TO_SURFACE, "depth" : 25 * mm, "endBoundEntityFace" : qUnion([Q3]), "offsetDistance" : 25 * mm});
        }
    });
